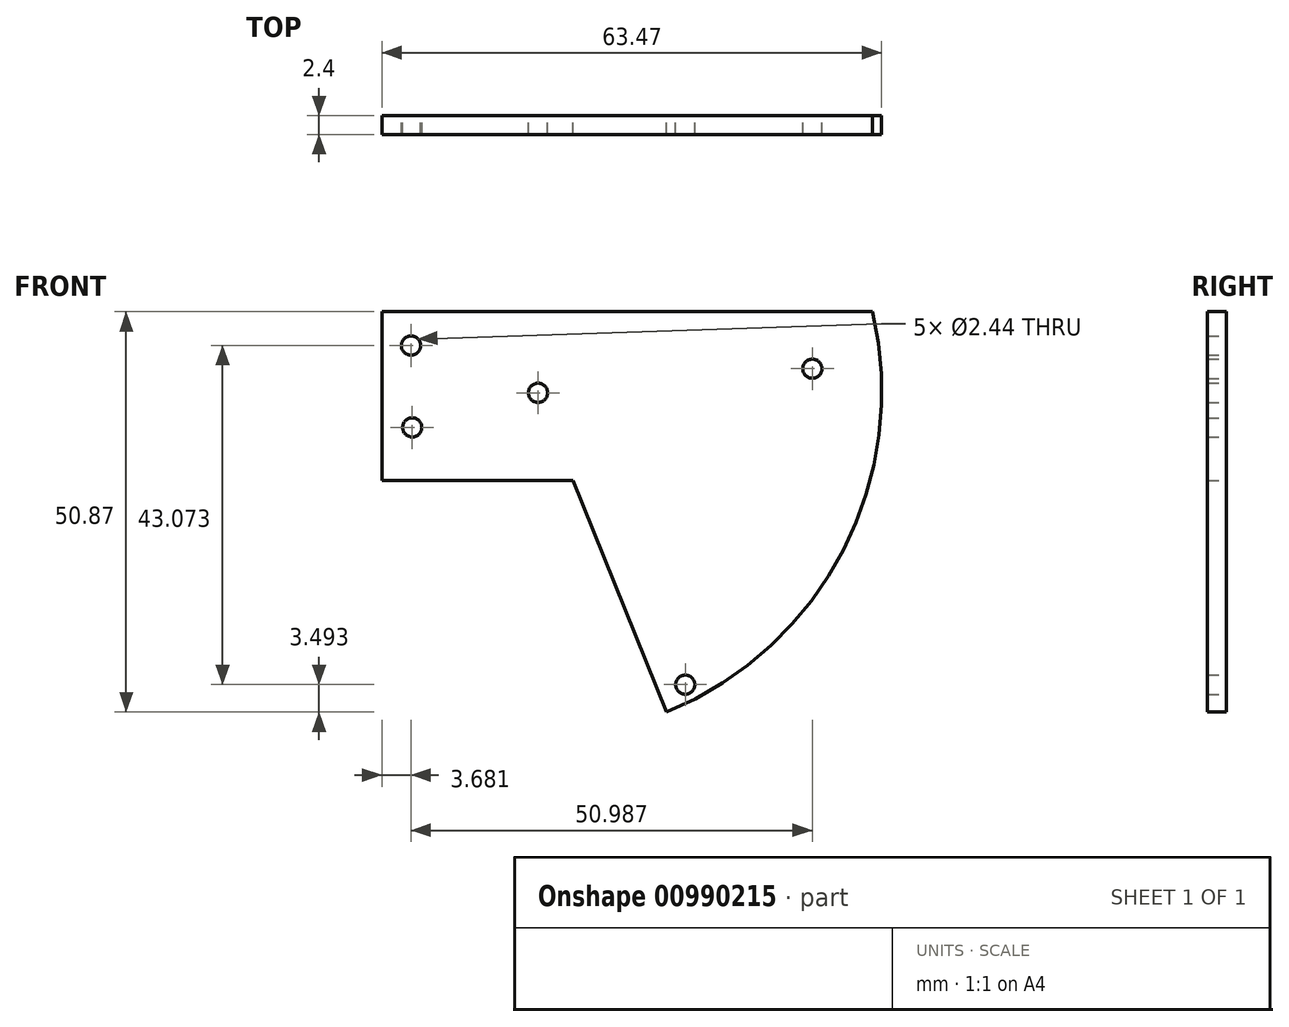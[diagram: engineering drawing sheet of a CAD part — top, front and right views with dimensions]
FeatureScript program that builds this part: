
annotation { "Feature Type Name" : "Feature", "Feature Type Description" : "" }
export const myFeature = defineFeature(function(context is Context, id is Id, definition is map)
    precondition{}
    {
        {
            var Q0;
            Q0=qCreatedBy(makeId("Front.planeOp"),FACE);
            var sketch = newSketch(context, id + "F0", { "sketchPlane" : qUnion([Q0])});
            skLineSegment(sketch, "E0", {"start": v(0, 21.44) * mm, "end": v(0, 0) * mm});
            skLineSegment(sketch, "E1", {"start": v(0, 21.44) * mm, "end": v(62.3, 21.44) * mm});
            skLineSegment(sketch, "E2", {"start": v(0, 0) * mm, "end": v(24.26, 0) * mm});
            skLineSegment(sketch, "E3", {"start": v(24.26, 0) * mm, "end": v(36.14, -29.43) * mm});
            skArc(sketch, "E4", {"start": v(36.14, -29.43) * mm, "mid": v(58.6, -8.82) * mm, "end": v(62.3, 21.44) * mm});
            skCircle(sketch, "E5", {"center": v(3.68, 17.14) * mm, "radius": 1.22 * mm});
            skCircle(sketch, "E6", {"center": v(3.84, 6.74) * mm, "radius": 1.22 * mm});
            skCircle(sketch, "E7", {"center": v(54.67, 14.2) * mm, "radius": 1.22 * mm});
            skCircle(sketch, "E8", {"center": v(38.52, -25.94) * mm, "radius": 1.22 * mm});
            skCircle(sketch, "E9", {"center": v(19.82, 11.13) * mm, "radius": 1.22 * mm});
            skSolve(sketch);
        }
        {
            var Q0;
            Q0=makeQuery(id+"F0.imprint","IMPRINT",FACE,{"disambiguationData":[TD([[makeQuery(id+"F0.imprint","IMPRINT",EDGE,{"derivedFrom":sQuery(id+"F0.wireOp",EDGE,"E0")}),1.0]])]});
            extrude(context, id + "F1", {"entities" : qUnion([Q0]), "depth" : 2.4 * mm, "offsetDistance" : 25 * mm});
        }
    });
